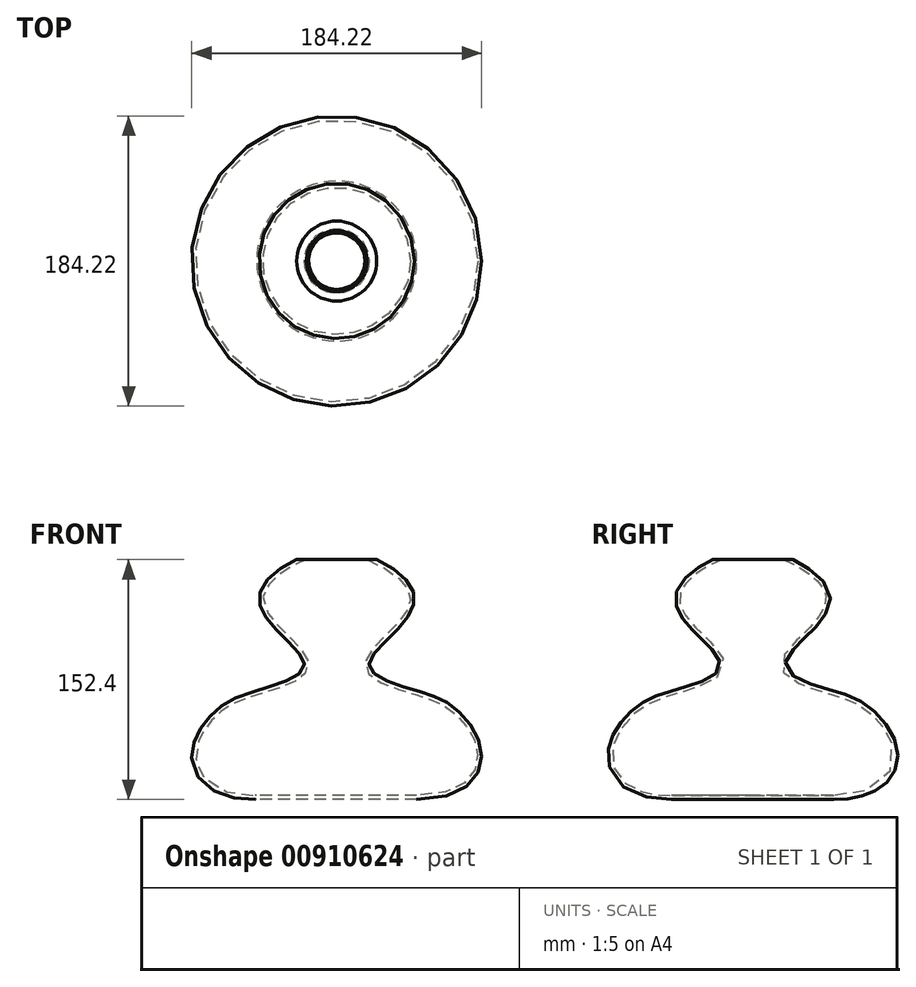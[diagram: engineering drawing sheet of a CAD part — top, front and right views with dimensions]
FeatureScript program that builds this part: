
annotation { "Feature Type Name" : "Feature", "Feature Type Description" : "" }
export const myFeature = defineFeature(function(context is Context, id is Id, definition is map)
    precondition{}
    {
        {
            var Q0;
            Q0=qCreatedBy(makeId("Front.planeOp"),FACE);
            var sketch = newSketch(context, id + "F0", { "sketchPlane" : qUnion([Q0])});
            skLineSegment(sketch, "E0", {"start": v(0, 0) * mm, "end": v(0, -152.4) * mm});
            skLineSegment(sketch, "E1", {"start": v(0, -152.4) * mm, "end": v(-50.8, -152.4) * mm});
            skLineSegment(sketch, "E2", {"start": v(0, 0) * mm, "end": v(-25.4, 0) * mm});
            skFitSpline(sketch, "E3", {"points": [v(-25.4, 0) * mm, v(-49.2, -23.08) * mm, v(-37.16, -45.72) * mm, v(-20.67, -68.07) * mm, v(-46, -81.88) * mm, v(-73.92, -93.62) * mm, v(-92.1, -124.32) * mm, v(-50.8, -152.4) * mm], "startDerivative": vector(-267.52, -124.05) * mm, "endDerivative": vector(504.79, 5.06) * mm});
            skSolve(sketch);
        }
        {
            var Q0;
            Q0 = qSketchRegion(id + "F0", true);
            var Q1;
            Q1=sQuery(id+"F0.wireOp",EDGE,"E0");
            revolve(context, id + "F1", {"surfaceOperationType" : NewSurfaceOperationType.NEW, "entities" : qUnion([Q0]), "axis" : qUnion([Q1]), "revolveType" : RevolveType.FULL});
        }
        {
            var Q0;
            Q0=makeQuery(id+"F1.opRevolve","SWEPT_FACE",FACE,{"disambiguationData":[OSD([sQuery(id+"F0.wireOp",EDGE,"E2")])]});
            shell(context, id + "F2", {"entities" : qUnion([Q0]), "thickness" : 2.54 * mm});
        }
    });
